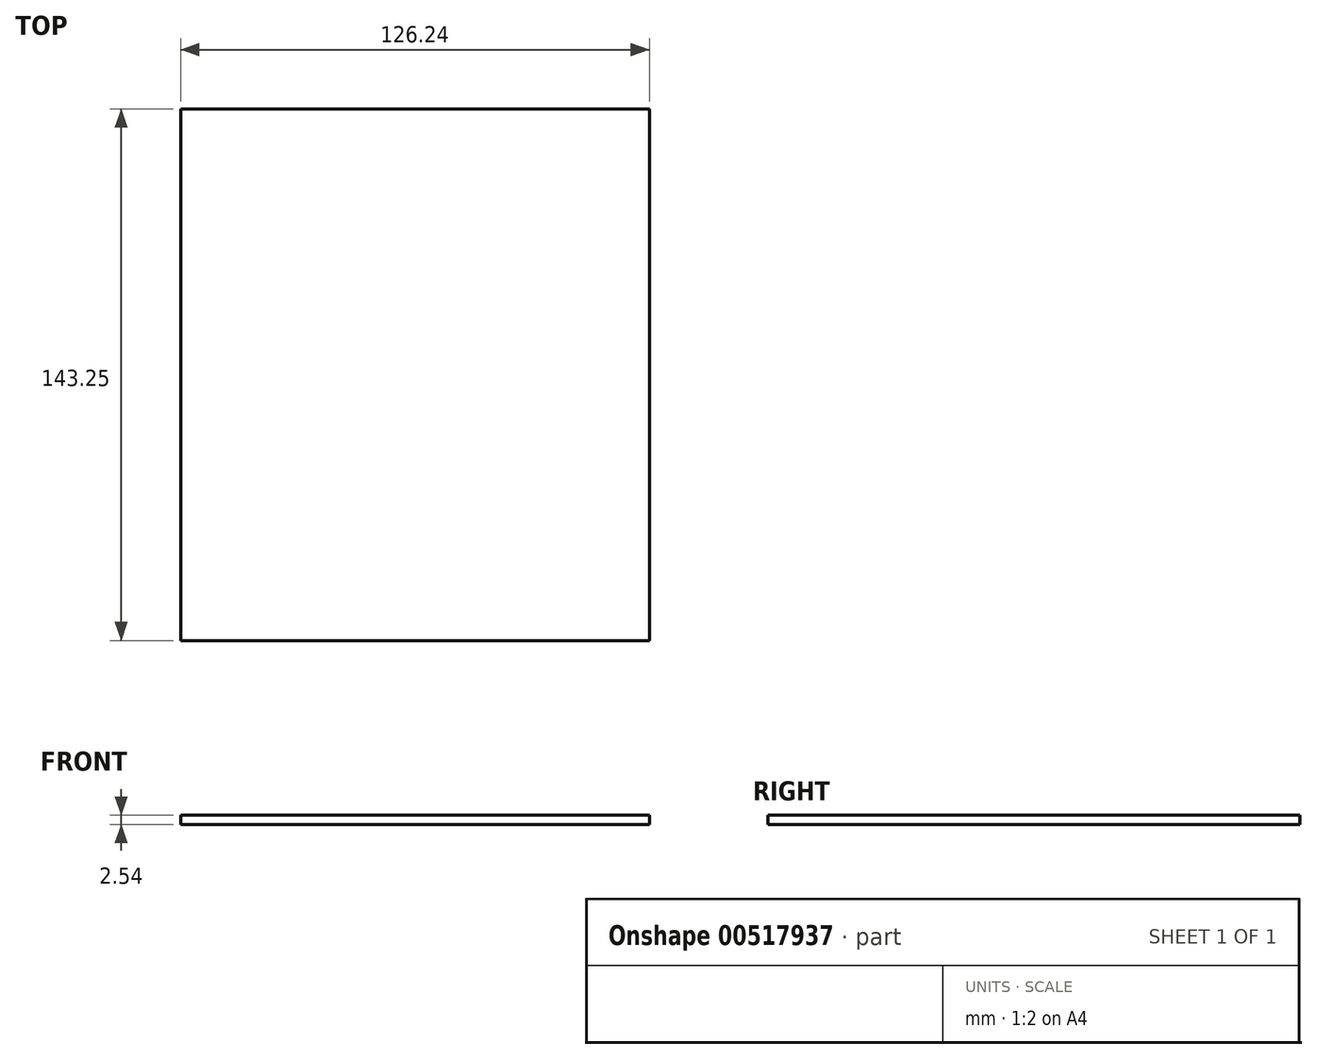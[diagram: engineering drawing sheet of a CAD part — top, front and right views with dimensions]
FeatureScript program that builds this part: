
annotation { "Feature Type Name" : "Feature", "Feature Type Description" : "" }
export const myFeature = defineFeature(function(context is Context, id is Id, definition is map)
    precondition{}
    {
        {
            var Q0;
            Q0=qCreatedBy(makeId("Top.planeOp"),FACE);
            var sketch = newSketch(context, id + "F0", { "sketchPlane" : qUnion([Q0])});
            skLineSegment(sketch, "E0", {"start": v(-71.45, 76.04) * mm, "end": v(-71.45, -67.21) * mm});
            skLineSegment(sketch, "E1", {"start": v(-71.45, -67.21) * mm, "end": v(54.8, -67.21) * mm});
            skLineSegment(sketch, "E2", {"start": v(54.8, -67.21) * mm, "end": v(54.8, 76.04) * mm});
            skLineSegment(sketch, "E3", {"start": v(54.8, 76.04) * mm, "end": v(-71.45, 76.04) * mm});
            skSolve(sketch);
        }
        {
            var Q0;
            Q0=makeQuery(id+"F0.imprint","IMPRINT",FACE,{"disambiguationData":[TD([[makeQuery(id+"F0.imprint","IMPRINT",EDGE,{"derivedFrom":sQuery(id+"F0.wireOp",EDGE,"E0")}),1.0]])]});
            extrude(context, id + "F1", {"entities" : qUnion([Q0]), "depth" : 2.54 * mm, "offsetDistance" : 25.4 * mm});
        }
    });
